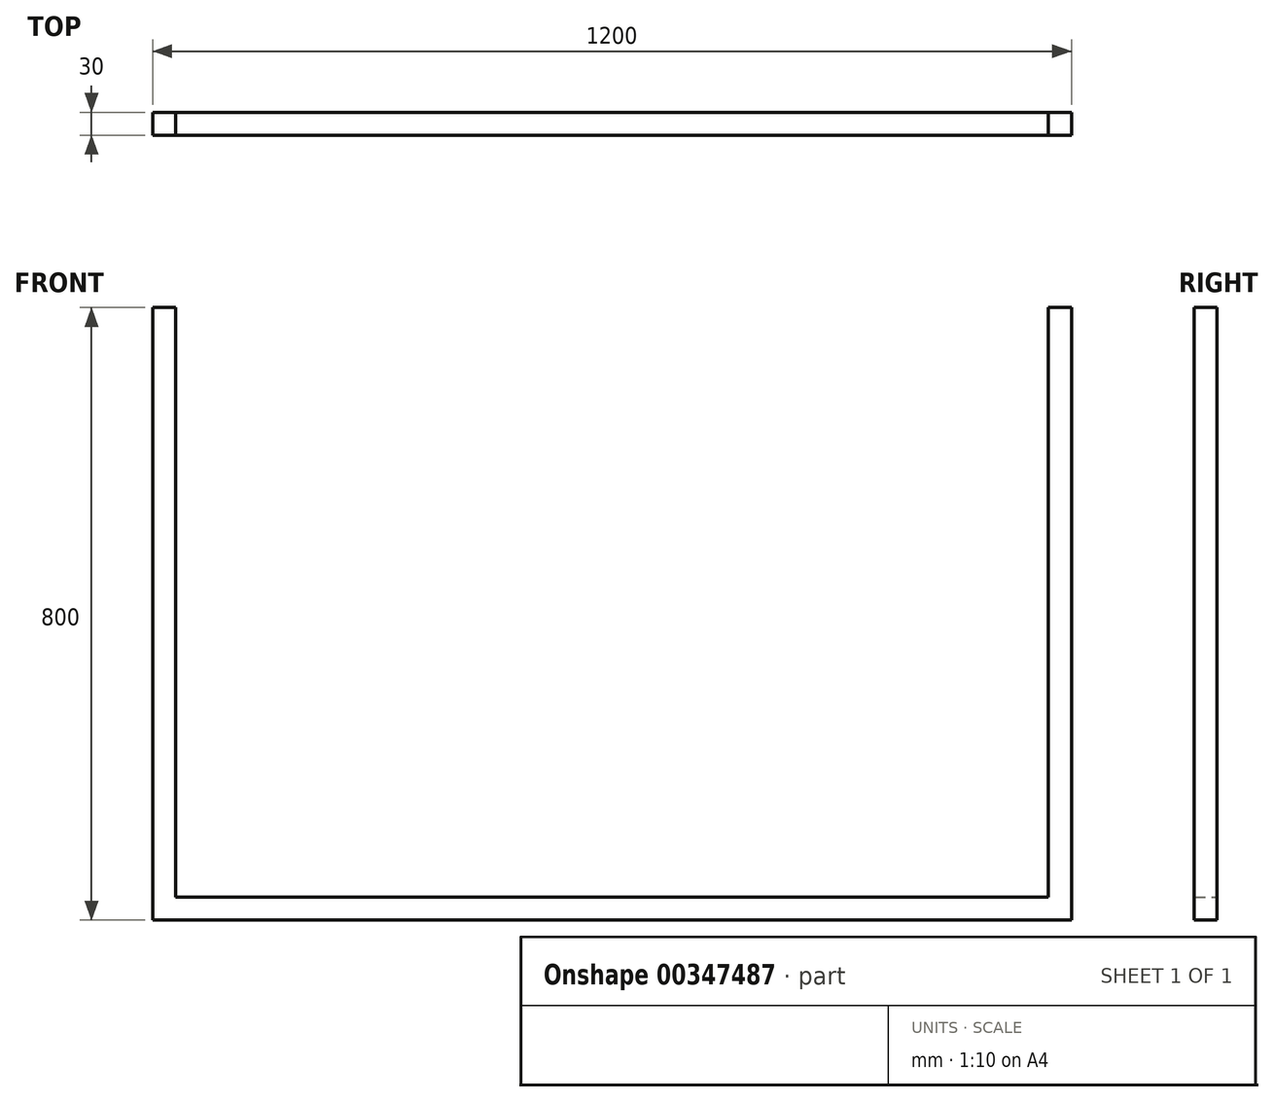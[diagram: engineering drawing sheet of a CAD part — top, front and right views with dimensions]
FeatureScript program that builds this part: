
annotation { "Feature Type Name" : "Feature", "Feature Type Description" : "" }
export const myFeature = defineFeature(function(context is Context, id is Id, definition is map)
    precondition{}
    {
        {
            var Q0;
            Q0=qCreatedBy(makeId("Front.planeOp"),FACE);
            var sketch = newSketch(context, id + "F0", { "sketchPlane" : qUnion([Q0])});
            skLineSegment(sketch, "E0.bottom", {"start": v(-51.71, 741.2) * mm, "end": v(-21.71, 741.2) * mm});
            skLineSegment(sketch, "E0.top", {"start": v(-51.71, -58.8) * mm, "end": v(1148.29, -58.8) * mm});
            skLineSegment(sketch, "E0.left", {"start": v(-51.71, 741.2) * mm, "end": v(-51.71, -58.8) * mm});
            skLineSegment(sketch, "E0.right", {"start": v(1148.29, 741.2) * mm, "end": v(1148.29, -58.8) * mm});
            skLineSegment(sketch, "E1.0", {"start": v(1118.29, 741.2) * mm, "end": v(1118.29, -28.8) * mm});
            skLineSegment(sketch, "E1.1", {"start": v(-21.71, -28.8) * mm, "end": v(1118.29, -28.8) * mm});
            skLineSegment(sketch, "E1.2", {"start": v(-21.71, 741.2) * mm, "end": v(-21.71, -28.8) * mm});
            skLineSegment(sketch, "E2.trimOffspring", {"start": v(1118.29, 741.2) * mm, "end": v(1148.29, 741.2) * mm});
            skSolve(sketch);
        }
        {
            var Q0;
            Q0 = qSketchRegion(id + "F0", true);
            extrude(context, id + "F1", {"entities" : qUnion([Q0]), "depth" : 30 * mm});
        }
    });
